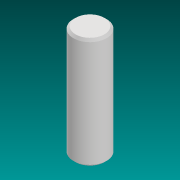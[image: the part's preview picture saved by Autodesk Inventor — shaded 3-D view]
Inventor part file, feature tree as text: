
AUTODESK INVENTOR PART (.ipt)
format: ipt  version: 2021 (Build 250183000, 183)  size: 81,408 bytes
history: native  units: mm
features: extrude x1, chamfer x1, sketch x1
ambient origin geometry x8: Origin, YZ Plane, XZ Plane, XY Plane, X Axis, Y Axis, Z Axis, Center Point
bodies: 实体1 (feature_tree)
feature tree (3):
  extrude  "拉伸1"  Depth=100.0mm TaperAngle=0.0deg
  chamfer  "倒角1"  Distance=2.0mm Angle=45.0deg
  sketch  "草图1"  dims[d0=30.0mm d1=100.0mm d2=0.0mm d3=2.0mm d4=2.0mm d5=45.0deg]
